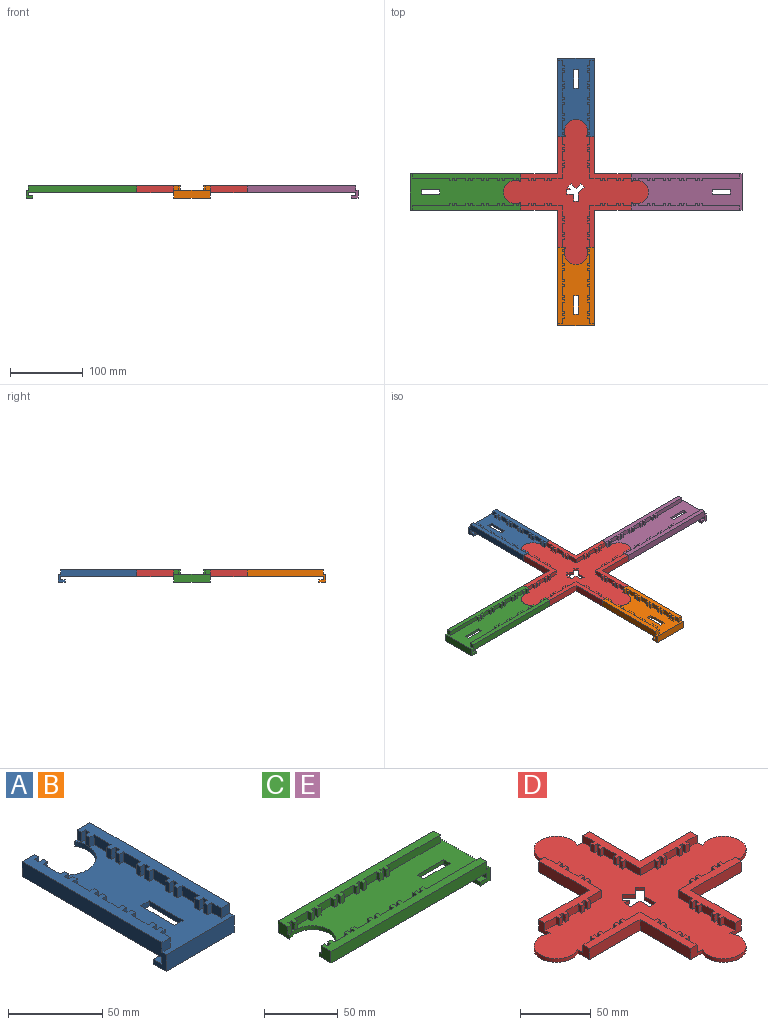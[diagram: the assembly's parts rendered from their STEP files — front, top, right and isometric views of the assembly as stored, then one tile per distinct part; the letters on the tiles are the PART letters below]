
ASSEMBLY  parts=5 mates=8
PART A: 100 faces, bbox 50.8x108x17.1 mm
  f0: plane 100.33x50.8mm, normal (0,0,1), area 3132.4mm2, adj f3,f4,f5,f6,f8,f10,f11,f12
  f1: plane 7.62x5.12mm, normal (0,0,1), area 14.9mm2, adj f8,f9,f94,f95,f96,f97,f98
  f2: plane 104.78x50.8mm, normal (0,0,-1), area 4533.1mm2, adj f3,f4,f5,f6,f7,f8,f9,f10
  f3: plane 25.4x3.18mm, normal (1,0,0), area 80.6mm2, adj f0,f2,f4,f12
  f4: plane 6.35x3.18mm, normal (0,-1,0), area 20.2mm2, adj f0,f2,f3,f5
  f5: plane 25.4x3.18mm, normal (-1,0,0), area 80.6mm2, adj f0,f2,f4,f12
  f6: plane 107.95x17.15mm, normal (1,0,0), area 1052.4mm2, adj f0,f2,f7,f11,f14,f15,f16,f17
  f7: plane 11.47x9.53mm, normal (0,1,0), area 96.9mm2, adj f2,f6,f8,f13,f18,f58
  f8: cylinder r=15.88mm len=31.75mm, axis (0,0,-1), area 208.8mm2, adj f0,f1,f2,f7,f9,f13
  f9: plane 11.47x9.53mm, normal (0,1,0), area 96.9mm2, adj f1,f2,f8,f10,f98,f99
  f10: plane 107.95x17.15mm, normal (-1,0,0), area 1052.4mm2, adj f0,f2,f9,f11,f14,f15,f16,f17
  f11: plane 50.8x10.8mm, normal (0,-1,0), area 548.4mm2, adj f0,f6,f10,f15
  f12: plane 6.35x3.18mm, normal (0,1,0), area 20.2mm2, adj f0,f2,f3,f5
  f13: plane 7.62x5.12mm, normal (0,0,1), area 14.9mm2, adj f7,f8,f18,f19,f20,f21,f22
  f14: plane 50.8x4.45mm, normal (0,1,0), area 225.8mm2, adj f2,f6,f10,f16
  f15: plane 50.8x9.53mm, normal (0,0,-1), area 483.9mm2, adj f6,f10,f11,f17
  f16: plane 50.8x6.35mm, normal (0,0,1), area 322.6mm2, adj f6,f10,f14,f17
  f17: plane 50.8x3.18mm, normal (0,1,0), area 161.3mm2, adj f6,f10,f15,f16
  f18: plane 6.35x3.18mm, normal (-1,0,0), area 20.2mm2, adj f7,f13,f19,f58
  f19: plane 6.35x3.18mm, normal (0,-1,0), area 20.2mm2, adj f13,f18,f20,f58
  f20: plane 6.35x3.18mm, normal (-1,0,0), area 20.2mm2, adj f13,f19,f21,f58
  f21: plane 6.35x3.18mm, normal (0,1,0), area 20.2mm2, adj f13,f20,f22,f58
  f22: plane 6.35x3.18mm, normal (-1,0,0), area 20.2mm2, adj f0,f13,f21,f23,f58
  f23: plane 6.35x3.18mm, normal (0,-1,0), area 20.2mm2, adj f0,f22,f24,f58
  f24: plane 12.7x6.35mm, normal (-1,0,0), area 80.6mm2, adj f0,f23,f25,f58
  f25: plane 6.35x3.18mm, normal (0,1,0), area 20.2mm2, adj f0,f24,f26,f58
  f26: plane 6.35x3.18mm, normal (-1,0,0), area 20.2mm2, adj f0,f25,f27,f58
  f27: plane 6.35x3.18mm, normal (0,-1,0), area 20.2mm2, adj f0,f26,f28,f58
  f28: plane 6.35x3.18mm, normal (-1,0,0), area 20.2mm2, adj f0,f27,f29,f58
  f29: plane 6.35x3.18mm, normal (0,1,0), area 20.2mm2, adj f0,f28,f30,f58
  f30: plane 6.35x3.18mm, normal (-1,0,0), area 20.2mm2, adj f0,f29,f31,f58
  f31: plane 6.35x3.18mm, normal (0,-1,0), area 20.2mm2, adj f0,f30,f32,f58
  f32: plane 12.7x6.35mm, normal (-1,0,0), area 80.6mm2, adj f0,f31,f33,f58
  f33: plane 6.35x3.18mm, normal (0,1,0), area 20.2mm2, adj f0,f32,f34,f58
  f34: plane 6.35x3.18mm, normal (-1,0,0), area 20.2mm2, adj f0,f33,f35,f58
  f35: plane 6.35x3.18mm, normal (0,-1,0), area 20.2mm2, adj f0,f34,f36,f58
  f36: plane 6.35x3.18mm, normal (-1,0,0), area 20.2mm2, adj f0,f35,f37,f58
  f37: plane 6.35x3.18mm, normal (0,1,0), area 20.2mm2, adj f0,f36,f38,f58
  f38: plane 6.35x3.18mm, normal (-1,0,0), area 20.2mm2, adj f0,f37,f39,f58
  f39: plane 6.35x3.18mm, normal (0,-1,0), area 20.2mm2, adj f0,f38,f40,f58
  f40: plane 11.91x6.35mm, normal (-1,0,0), area 75.6mm2, adj f0,f39,f41,f58
  f41: plane 6.35x3.18mm, normal (0,1,0), area 20.2mm2, adj f0,f40,f42,f58
  f42: plane 6.35x3.18mm, normal (-1,0,0), area 20.2mm2, adj f0,f41,f43,f58
  f43: plane 6.35x3.18mm, normal (0,-1,0), area 20.2mm2, adj f0,f42,f44,f58
  f44: plane 6.35x3.18mm, normal (-1,0,0), area 20.2mm2, adj f0,f43,f45,f58
  f45: plane 6.35x3.18mm, normal (0,1,0), area 20.2mm2, adj f0,f44,f46,f58
  f46: plane 6.35x3.18mm, normal (-1,0,0), area 20.2mm2, adj f0,f45,f47,f58
  f47: plane 6.35x3.18mm, normal (0,-1,0), area 20.2mm2, adj f0,f46,f48,f58
  f48: plane 12.7x6.35mm, normal (-1,0,0), area 80.6mm2, adj f0,f47,f49,f58
  f49: plane 6.35x3.18mm, normal (0,1,0), area 20.2mm2, adj f0,f48,f50,f58
  f50: plane 6.35x3.18mm, normal (-1,0,0), area 20.2mm2, adj f0,f49,f51,f58
  f51: plane 6.35x3.18mm, normal (0,-1,0), area 20.2mm2, adj f0,f50,f52,f58
  f52: plane 6.35x3.18mm, normal (-1,0,0), area 20.2mm2, adj f0,f51,f53,f58
  f53: plane 6.35x3.18mm, normal (0,1,0), area 20.2mm2, adj f0,f52,f54,f58
  f54: plane 6.35x3.18mm, normal (-1,0,0), area 20.2mm2, adj f0,f53,f55,f58
  f55: plane 6.35x3.18mm, normal (0,-1,0), area 20.2mm2, adj f0,f54,f56,f58
  f56: plane 7.14x6.35mm, normal (-1,0,0), area 45.4mm2, adj f0,f55,f57,f58
  f57: plane 6.35x6.35mm, normal (0,-1,0), area 40.3mm2, adj f0,f6,f56,f58
  f58: plane 104.78x9.53mm, normal (0,0,1), area 766.1mm2, adj f6,f7,f18,f19,f20,f21,f22,f23
  f59: plane 6.35x6.35mm, normal (0,-1,0), area 40.3mm2, adj f0,f10,f60,f99
  f60: plane 7.14x6.35mm, normal (1,0,0), area 45.4mm2, adj f0,f59,f61,f99
  f61: plane 6.35x3.18mm, normal (0,-1,0), area 20.2mm2, adj f0,f60,f62,f99
  f62: plane 6.35x3.18mm, normal (1,0,0), area 20.2mm2, adj f0,f61,f63,f99
  f63: plane 6.35x3.18mm, normal (0,1,0), area 20.2mm2, adj f0,f62,f64,f99
  f64: plane 6.35x3.18mm, normal (1,0,0), area 20.2mm2, adj f0,f63,f65,f99
  f65: plane 6.35x3.18mm, normal (0,-1,0), area 20.2mm2, adj f0,f64,f66,f99
  f66: plane 6.35x3.18mm, normal (1,0,0), area 20.2mm2, adj f0,f65,f67,f99
  f67: plane 6.35x3.18mm, normal (0,1,0), area 20.2mm2, adj f0,f66,f68,f99
  f68: plane 12.7x6.35mm, normal (1,0,0), area 80.6mm2, adj f0,f67,f69,f99
  f69: plane 6.35x3.18mm, normal (0,-1,0), area 20.2mm2, adj f0,f68,f70,f99
  f70: plane 6.35x3.18mm, normal (1,0,0), area 20.2mm2, adj f0,f69,f71,f99
  f71: plane 6.35x3.18mm, normal (0,1,0), area 20.2mm2, adj f0,f70,f72,f99
  f72: plane 6.35x3.18mm, normal (1,0,0), area 20.2mm2, adj f0,f71,f73,f99
  f73: plane 6.35x3.18mm, normal (0,-1,0), area 20.2mm2, adj f0,f72,f74,f99
  f74: plane 6.35x3.18mm, normal (1,0,0), area 20.2mm2, adj f0,f73,f75,f99
  f75: plane 6.35x3.18mm, normal (0,1,0), area 20.2mm2, adj f0,f74,f76,f99
  f76: plane 11.91x6.35mm, normal (1,0,0), area 75.6mm2, adj f0,f75,f77,f99
  f77: plane 6.35x3.18mm, normal (0,-1,0), area 20.2mm2, adj f0,f76,f78,f99
  f78: plane 6.35x3.18mm, normal (1,0,0), area 20.2mm2, adj f0,f77,f79,f99
  f79: plane 6.35x3.18mm, normal (0,1,0), area 20.2mm2, adj f0,f78,f80,f99
  f80: plane 6.35x3.18mm, normal (1,0,0), area 20.2mm2, adj f0,f79,f81,f99
  f81: plane 6.35x3.18mm, normal (0,-1,0), area 20.2mm2, adj f0,f80,f82,f99
  f82: plane 6.35x3.18mm, normal (1,0,0), area 20.2mm2, adj f0,f81,f83,f99
  f83: plane 6.35x3.18mm, normal (0,1,0), area 20.2mm2, adj f0,f82,f84,f99
  f84: plane 12.7x6.35mm, normal (1,0,0), area 80.6mm2, adj f0,f83,f85,f99
  f85: plane 6.35x3.18mm, normal (0,-1,0), area 20.2mm2, adj f0,f84,f86,f99
  f86: plane 6.35x3.18mm, normal (1,0,0), area 20.2mm2, adj f0,f85,f87,f99
  f87: plane 6.35x3.18mm, normal (0,1,0), area 20.2mm2, adj f0,f86,f88,f99
  f88: plane 6.35x3.18mm, normal (1,0,0), area 20.2mm2, adj f0,f87,f89,f99
  f89: plane 6.35x3.18mm, normal (0,-1,0), area 20.2mm2, adj f0,f88,f90,f99
  f90: plane 6.35x3.18mm, normal (1,0,0), area 20.2mm2, adj f0,f89,f91,f99
  f91: plane 6.35x3.18mm, normal (0,1,0), area 20.2mm2, adj f0,f90,f92,f99
  f92: plane 12.7x6.35mm, normal (1,0,0), area 80.6mm2, adj f0,f91,f93,f99
  f93: plane 6.35x3.18mm, normal (0,-1,0), area 20.2mm2, adj f0,f92,f94,f99
  f94: plane 6.35x3.18mm, normal (1,0,0), area 20.2mm2, adj f0,f1,f93,f95,f99
  f95: plane 6.35x3.18mm, normal (0,1,0), area 20.2mm2, adj f1,f94,f96,f99
  f96: plane 6.35x3.18mm, normal (1,0,0), area 20.2mm2, adj f1,f95,f97,f99
  f97: plane 6.35x3.18mm, normal (0,-1,0), area 20.2mm2, adj f1,f96,f98,f99
  f98: plane 6.35x3.18mm, normal (1,0,0), area 20.2mm2, adj f1,f9,f97,f99
  f99: plane 104.78x9.53mm, normal (0,0,1), area 766.1mm2, adj f9,f10,f59,f60,f61,f62,f63,f64
PART B: same geometry as A
PART C: 100 faces, bbox 152.4x50.8x17.1 mm
  f0: plane 144.78x50.8mm, normal (0,0,1), area 4825.9mm2, adj f3,f4,f5,f6,f8,f10,f11,f12
  f1: plane 7.62x5.12mm, normal (0,0,1), area 14.9mm2, adj f8,f9,f94,f95,f96,f97,f98
  f2: plane 50.8x4.45mm, normal (-1,0,0), area 225.8mm2, adj f6,f10,f14,f16
  f3: plane 6.35x3.18mm, normal (1,0,0), area 20.2mm2, adj f0,f4,f12,f14
  f4: plane 25.4x3.18mm, normal (0,-1,0), area 80.6mm2, adj f0,f3,f5,f14
  f5: plane 6.35x3.18mm, normal (-1,0,0), area 20.2mm2, adj f0,f4,f12,f14
  f6: plane 152.4x17.15mm, normal (0,1,0), area 1475.8mm2, adj f0,f2,f7,f11,f14,f15,f16,f17
  f7: plane 11.47x9.53mm, normal (-1,0,0), area 96.9mm2, adj f6,f8,f13,f14,f19,f58
  f8: cylinder r=15.88mm len=31.75mm, axis (0,0,-1), area 208.8mm2, adj f0,f1,f7,f9,f13,f14
  f9: plane 11.47x9.53mm, normal (-1,0,0), area 96.9mm2, adj f1,f8,f10,f14,f98,f99
  f10: plane 152.4x17.15mm, normal (0,-1,0), area 1475.8mm2, adj f0,f2,f9,f11,f14,f15,f16,f17
  f11: plane 50.8x10.8mm, normal (1,0,0), area 548.4mm2, adj f0,f6,f10,f15
  f12: plane 25.4x3.18mm, normal (0,1,0), area 80.6mm2, adj f0,f3,f5,f14
  f13: plane 7.62x5.12mm, normal (0,0,1), area 14.9mm2, adj f7,f8,f19,f20,f21,f22,f23
  f14: plane 149.23x50.8mm, normal (0,0,-1), area 6791.2mm2, adj f2,f3,f4,f5,f6,f7,f8,f9
  f15: plane 50.8x9.53mm, normal (0,0,-1), area 483.9mm2, adj f6,f10,f11,f17
  f16: plane 50.8x6.35mm, normal (0,0,1), area 322.6mm2, adj f2,f6,f10,f17
  f17: plane 50.8x3.18mm, normal (-1,0,0), area 161.3mm2, adj f6,f10,f15,f16
  f18: plane 6.35x6.35mm, normal (1,0,0), area 40.3mm2, adj f0,f6,f57,f58
  f19: plane 6.35x3.18mm, normal (0,-1,0), area 20.2mm2, adj f7,f13,f20,f58
  f20: plane 6.35x3.18mm, normal (1,0,0), area 20.2mm2, adj f13,f19,f21,f58
  f21: plane 6.35x3.18mm, normal (0,-1,0), area 20.2mm2, adj f13,f20,f22,f58
  f22: plane 6.35x3.18mm, normal (-1,0,0), area 20.2mm2, adj f13,f21,f23,f58
  f23: plane 6.35x3.18mm, normal (0,-1,0), area 20.2mm2, adj f0,f13,f22,f24,f58
  f24: plane 6.35x3.18mm, normal (1,0,0), area 20.2mm2, adj f0,f23,f25,f58
  f25: plane 12.7x6.35mm, normal (0,-1,0), area 80.6mm2, adj f0,f24,f26,f58
  f26: plane 6.35x3.18mm, normal (-1,0,0), area 20.2mm2, adj f0,f25,f27,f58
  f27: plane 6.35x3.18mm, normal (0,-1,0), area 20.2mm2, adj f0,f26,f28,f58
  f28: plane 6.35x3.18mm, normal (1,0,0), area 20.2mm2, adj f0,f27,f29,f58
  f29: plane 6.35x3.18mm, normal (0,-1,0), area 20.2mm2, adj f0,f28,f30,f58
  f30: plane 6.35x3.18mm, normal (-1,0,0), area 20.2mm2, adj f0,f29,f31,f58
  f31: plane 6.35x3.18mm, normal (0,-1,0), area 20.2mm2, adj f0,f30,f32,f58
  f32: plane 6.35x3.18mm, normal (1,0,0), area 20.2mm2, adj f0,f31,f33,f58
  f33: plane 12.7x6.35mm, normal (0,-1,0), area 80.6mm2, adj f0,f32,f34,f58
  f34: plane 6.35x3.18mm, normal (-1,0,0), area 20.2mm2, adj f0,f33,f35,f58
  f35: plane 6.35x3.18mm, normal (0,-1,0), area 20.2mm2, adj f0,f34,f36,f58
  f36: plane 6.35x3.18mm, normal (1,0,0), area 20.2mm2, adj f0,f35,f37,f58
  f37: plane 6.35x3.18mm, normal (0,-1,0), area 20.2mm2, adj f0,f36,f38,f58
  f38: plane 6.35x3.18mm, normal (-1,0,0), area 20.2mm2, adj f0,f37,f39,f58
  f39: plane 6.35x3.18mm, normal (0,-1,0), area 20.2mm2, adj f0,f38,f40,f58
  f40: plane 6.35x3.18mm, normal (1,0,0), area 20.2mm2, adj f0,f39,f41,f58
  f41: plane 11.91x6.35mm, normal (0,-1,0), area 75.6mm2, adj f0,f40,f42,f58
  f42: plane 6.35x3.18mm, normal (-1,0,0), area 20.2mm2, adj f0,f41,f43,f58
  f43: plane 6.35x3.18mm, normal (0,-1,0), area 20.2mm2, adj f0,f42,f44,f58
  f44: plane 6.35x3.18mm, normal (1,0,0), area 20.2mm2, adj f0,f43,f45,f58
  f45: plane 6.35x3.18mm, normal (0,-1,0), area 20.2mm2, adj f0,f44,f46,f58
  f46: plane 6.35x3.18mm, normal (-1,0,0), area 20.2mm2, adj f0,f45,f47,f58
  f47: plane 6.35x3.18mm, normal (0,-1,0), area 20.2mm2, adj f0,f46,f48,f58
  f48: plane 6.35x3.18mm, normal (1,0,0), area 20.2mm2, adj f0,f47,f49,f58
  f49: plane 12.7x6.35mm, normal (0,-1,0), area 80.6mm2, adj f0,f48,f50,f58
  f50: plane 6.35x3.18mm, normal (-1,0,0), area 20.2mm2, adj f0,f49,f51,f58
  f51: plane 6.35x3.18mm, normal (0,-1,0), area 20.2mm2, adj f0,f50,f52,f58
  f52: plane 6.35x3.18mm, normal (1,0,0), area 20.2mm2, adj f0,f51,f53,f58
  f53: plane 6.35x3.18mm, normal (0,-1,0), area 20.2mm2, adj f0,f52,f54,f58
  f54: plane 6.35x3.18mm, normal (-1,0,0), area 20.2mm2, adj f0,f53,f55,f58
  f55: plane 6.35x3.18mm, normal (0,-1,0), area 20.2mm2, adj f0,f54,f56,f58
  f56: plane 6.35x3.18mm, normal (1,0,0), area 20.2mm2, adj f0,f55,f57,f58
  f57: plane 51.59x6.35mm, normal (0,-1,0), area 327.6mm2, adj f0,f18,f56,f58
  f58: plane 149.23x9.53mm, normal (0,0,1), area 1048.4mm2, adj f6,f7,f18,f19,f20,f21,f22,f23
  f59: plane 6.35x6.35mm, normal (1,0,0), area 40.3mm2, adj f0,f10,f60,f99
  f60: plane 51.59x6.35mm, normal (0,1,0), area 327.6mm2, adj f0,f59,f61,f99
  f61: plane 6.35x3.18mm, normal (1,0,0), area 20.2mm2, adj f0,f60,f62,f99
  f62: plane 6.35x3.18mm, normal (0,1,0), area 20.2mm2, adj f0,f61,f63,f99
  f63: plane 6.35x3.18mm, normal (-1,0,0), area 20.2mm2, adj f0,f62,f64,f99
  f64: plane 6.35x3.18mm, normal (0,1,0), area 20.2mm2, adj f0,f63,f65,f99
  f65: plane 6.35x3.18mm, normal (1,0,0), area 20.2mm2, adj f0,f64,f66,f99
  f66: plane 6.35x3.18mm, normal (0,1,0), area 20.2mm2, adj f0,f65,f67,f99
  f67: plane 6.35x3.18mm, normal (-1,0,0), area 20.2mm2, adj f0,f66,f68,f99
  f68: plane 12.7x6.35mm, normal (0,1,0), area 80.6mm2, adj f0,f67,f69,f99
  f69: plane 6.35x3.18mm, normal (1,0,0), area 20.2mm2, adj f0,f68,f70,f99
  f70: plane 6.35x3.18mm, normal (0,1,0), area 20.2mm2, adj f0,f69,f71,f99
  f71: plane 6.35x3.18mm, normal (-1,0,0), area 20.2mm2, adj f0,f70,f72,f99
  f72: plane 6.35x3.18mm, normal (0,1,0), area 20.2mm2, adj f0,f71,f73,f99
  f73: plane 6.35x3.18mm, normal (1,0,0), area 20.2mm2, adj f0,f72,f74,f99
  f74: plane 6.35x3.18mm, normal (0,1,0), area 20.2mm2, adj f0,f73,f75,f99
  f75: plane 6.35x3.18mm, normal (-1,0,0), area 20.2mm2, adj f0,f74,f76,f99
  f76: plane 11.91x6.35mm, normal (0,1,0), area 75.6mm2, adj f0,f75,f77,f99
  f77: plane 6.35x3.18mm, normal (1,0,0), area 20.2mm2, adj f0,f76,f78,f99
  f78: plane 6.35x3.18mm, normal (0,1,0), area 20.2mm2, adj f0,f77,f79,f99
  f79: plane 6.35x3.18mm, normal (-1,0,0), area 20.2mm2, adj f0,f78,f80,f99
  f80: plane 6.35x3.18mm, normal (0,1,0), area 20.2mm2, adj f0,f79,f81,f99
  f81: plane 6.35x3.18mm, normal (1,0,0), area 20.2mm2, adj f0,f80,f82,f99
  f82: plane 6.35x3.18mm, normal (0,1,0), area 20.2mm2, adj f0,f81,f83,f99
  f83: plane 6.35x3.18mm, normal (-1,0,0), area 20.2mm2, adj f0,f82,f84,f99
  f84: plane 12.7x6.35mm, normal (0,1,0), area 80.6mm2, adj f0,f83,f85,f99
  f85: plane 6.35x3.18mm, normal (1,0,0), area 20.2mm2, adj f0,f84,f86,f99
  f86: plane 6.35x3.18mm, normal (0,1,0), area 20.2mm2, adj f0,f85,f87,f99
  f87: plane 6.35x3.18mm, normal (-1,0,0), area 20.2mm2, adj f0,f86,f88,f99
  f88: plane 6.35x3.18mm, normal (0,1,0), area 20.2mm2, adj f0,f87,f89,f99
  f89: plane 6.35x3.18mm, normal (1,0,0), area 20.2mm2, adj f0,f88,f90,f99
  f90: plane 6.35x3.18mm, normal (0,1,0), area 20.2mm2, adj f0,f89,f91,f99
  f91: plane 6.35x3.18mm, normal (-1,0,0), area 20.2mm2, adj f0,f90,f92,f99
  f92: plane 12.7x6.35mm, normal (0,1,0), area 80.6mm2, adj f0,f91,f93,f99
  f93: plane 6.35x3.18mm, normal (1,0,0), area 20.2mm2, adj f0,f92,f94,f99
  f94: plane 6.35x3.18mm, normal (0,1,0), area 20.2mm2, adj f0,f1,f93,f95,f99
  f95: plane 6.35x3.18mm, normal (-1,0,0), area 20.2mm2, adj f1,f94,f96,f99
  f96: plane 6.35x3.18mm, normal (0,1,0), area 20.2mm2, adj f1,f95,f97,f99
  f97: plane 6.35x3.18mm, normal (1,0,0), area 20.2mm2, adj f1,f96,f98,f99
  f98: plane 6.35x3.18mm, normal (0,1,0), area 20.2mm2, adj f1,f9,f97,f99
  f99: plane 149.23x9.53mm, normal (0,0,1), area 1048.4mm2, adj f9,f10,f59,f60,f61,f62,f63,f64
PART D: 174 faces, bbox 199.4x199.4x9.5 mm
  f0: plane 199.39x199.39mm, normal (0,0,1), area 12077.4mm2, adj f1,f2,f3,f4,f5,f6,f7,f8
  f1: plane 4.49x4.49mm, normal (-0.71,-0.71,0), area 20.2mm2, adj f0,f2,f32,f33
  f2: plane 8.05x8.05mm, normal (-0.71,0.71,0), area 36.1mm2, adj f0,f1,f3,f33
  f3: plane 11.39x3.18mm, normal (-1,0,0), area 36.1mm2, adj f0,f2,f4,f33
  f4: plane 6.35x3.18mm, normal (0,1,0), area 20.2mm2, adj f0,f3,f5,f33
  f5: plane 9.53x3.18mm, normal (1,0,0), area 30.2mm2, adj f0,f4,f6,f33
  f6: plane 9.53x3.18mm, normal (0,1,0), area 30.2mm2, adj f0,f5,f7,f33
  f7: plane 6.35x3.18mm, normal (1,0,0), area 20.2mm2, adj f0,f6,f8,f33
  f8: plane 5.04x3.18mm, normal (0,-1,0), area 16mm2, adj f0,f7,f9,f33
  f9: plane 3.56x3.56mm, normal (0.71,0.71,0), area 16mm2, adj f0,f8,f10,f33
  f10: plane 4.49x4.49mm, normal (0.71,-0.71,0), area 20.2mm2, adj f0,f9,f11,f33
  f11: plane 6.74x6.74mm, normal (-0.71,-0.71,0), area 30.2mm2, adj f0,f10,f32,f33
  f12: cylinder r=15.88mm len=31.75mm, axis (0,0,-1), area 208.8mm2, adj f0,f13,f31,f33
  f13: plane 11.47x9.53mm, normal (-1,0,0), area 76.8mm2, adj f0,f12,f14,f33,f102,f103
  f14: plane 50.8x9.53mm, normal (0,-1,0), area 483.9mm2, adj f13,f15,f33,f103
  f15: plane 50.8x9.53mm, normal (-1,0,0), area 483.9mm2, adj f14,f16,f33,f103
  f16: plane 11.47x9.53mm, normal (0,-1,0), area 76.8mm2, adj f0,f15,f17,f33,f69,f103
  f17: cylinder r=15.88mm len=31.75mm, axis (0,0,-1), area 208.8mm2, adj f0,f16,f18,f33
  f18: plane 11.47x9.53mm, normal (0,-1,0), area 76.8mm2, adj f0,f17,f19,f33,f140,f173
  f19: plane 50.8x9.53mm, normal (1,0,0), area 483.9mm2, adj f18,f20,f33,f173
  f20: plane 50.8x9.53mm, normal (0,-1,0), area 483.9mm2, adj f19,f21,f33,f173
  f21: plane 11.47x9.53mm, normal (1,0,0), area 76.8mm2, adj f0,f20,f22,f33,f141,f173
  f22: cylinder r=15.88mm len=31.75mm, axis (0,0,-1), area 208.8mm2, adj f0,f21,f23,f33
  f23: plane 11.47x9.53mm, normal (1,0,0), area 76.8mm2, adj f0,f22,f24,f33,f137,f138
  f24: plane 50.8x9.53mm, normal (0,1,0), area 483.9mm2, adj f23,f25,f33,f138
  f25: plane 50.8x9.53mm, normal (1,0,0), area 483.9mm2, adj f24,f26,f33,f138
  f26: plane 11.47x9.53mm, normal (0,1,0), area 76.8mm2, adj f0,f25,f27,f33,f104,f138
  f27: cylinder r=15.88mm len=31.75mm, axis (0,0,-1), area 208.8mm2, adj f0,f26,f28,f33
  f28: plane 11.47x9.53mm, normal (0,1,0), area 76.8mm2, adj f0,f27,f29,f33,f50,f68
  f29: plane 50.8x9.53mm, normal (-1,0,0), area 483.9mm2, adj f28,f30,f33,f68
  f30: plane 50.8x9.53mm, normal (0,1,0), area 483.9mm2, adj f29,f31,f33,f68
  f31: plane 11.47x9.53mm, normal (-1,0,0), area 76.8mm2, adj f0,f12,f30,f33,f51,f68
  f32: plane 6.74x6.74mm, normal (0.71,-0.71,0), area 30.2mm2, adj f0,f1,f11,f33
  f33: plane 199.39x199.39mm, normal (0,0,-1), area 15141.9mm2, adj f1,f2,f3,f4,f5,f6,f7,f8
  f34: plane 14.29x6.35mm, normal (1,0,0), area 90.7mm2, adj f0,f35,f67,f68
  f35: plane 6.35x3.18mm, normal (0,-1,0), area 20.2mm2, adj f0,f34,f36,f68
  f36: plane 6.35x3.18mm, normal (1,0,0), area 20.2mm2, adj f0,f35,f37,f68
  f37: plane 6.35x3.18mm, normal (0,1,0), area 20.2mm2, adj f0,f36,f38,f68
  f38: plane 6.35x3.18mm, normal (1,0,0), area 20.2mm2, adj f0,f37,f39,f68
  f39: plane 6.35x3.18mm, normal (0,-1,0), area 20.2mm2, adj f0,f38,f40,f68
  f40: plane 6.35x3.18mm, normal (1,0,0), area 20.2mm2, adj f0,f39,f41,f68
  f41: plane 6.35x3.18mm, normal (0,1,0), area 20.2mm2, adj f0,f40,f42,f68
  f42: plane 12.7x6.35mm, normal (1,0,0), area 80.6mm2, adj f0,f41,f43,f68
  f43: plane 6.35x3.18mm, normal (0,-1,0), area 20.2mm2, adj f0,f42,f44,f68
  f44: plane 6.35x3.18mm, normal (1,0,0), area 20.2mm2, adj f0,f43,f45,f68
  f45: plane 6.35x3.18mm, normal (0,1,0), area 20.2mm2, adj f0,f44,f46,f68
  f46: plane 6.35x3.18mm, normal (1,0,0), area 20.2mm2, adj f0,f45,f47,f68
  f47: plane 6.35x3.18mm, normal (0,-1,0), area 20.2mm2, adj f0,f46,f48,f68
  f48: plane 6.35x3.18mm, normal (1,0,0), area 20.2mm2, adj f0,f47,f49,f68
  f49: plane 6.35x3.18mm, normal (0,1,0), area 20.2mm2, adj f0,f48,f50,f68
  f50: plane 11.11x6.35mm, normal (1,0,0), area 70.6mm2, adj f0,f28,f49,f68
  f51: plane 11.11x6.35mm, normal (0,-1,0), area 70.6mm2, adj f0,f31,f52,f68
  f52: plane 6.35x3.18mm, normal (-1,0,0), area 20.2mm2, adj f0,f51,f53,f68
  f53: plane 6.35x3.18mm, normal (0,-1,0), area 20.2mm2, adj f0,f52,f54,f68
  f54: plane 6.35x3.18mm, normal (1,0,0), area 20.2mm2, adj f0,f53,f55,f68
  f55: plane 6.35x3.18mm, normal (0,-1,0), area 20.2mm2, adj f0,f54,f56,f68
  f56: plane 6.35x3.18mm, normal (-1,0,0), area 20.2mm2, adj f0,f55,f57,f68
  f57: plane 6.35x3.18mm, normal (0,-1,0), area 20.2mm2, adj f0,f56,f58,f68
  f58: plane 6.35x3.18mm, normal (1,0,0), area 20.2mm2, adj f0,f57,f59,f68
  f59: plane 12.7x6.35mm, normal (0,-1,0), area 80.6mm2, adj f0,f58,f60,f68
  f60: plane 6.35x3.18mm, normal (-1,0,0), area 20.2mm2, adj f0,f59,f61,f68
  f61: plane 6.35x3.18mm, normal (0,-1,0), area 20.2mm2, adj f0,f60,f62,f68
  f62: plane 6.35x3.18mm, normal (1,0,0), area 20.2mm2, adj f0,f61,f63,f68
  f63: plane 6.35x3.18mm, normal (0,-1,0), area 20.2mm2, adj f0,f62,f64,f68
  f64: plane 6.35x3.18mm, normal (-1,0,0), area 20.2mm2, adj f0,f63,f65,f68
  f65: plane 6.35x3.18mm, normal (0,-1,0), area 20.2mm2, adj f0,f64,f66,f68
  f66: plane 6.35x3.18mm, normal (1,0,0), area 20.2mm2, adj f0,f65,f67,f68
  f67: plane 14.29x6.35mm, normal (0,-1,0), area 90.7mm2, adj f0,f34,f66,f68
  f68: plane 60.33x60.33mm, normal (0,0,1), area 766.1mm2, adj f28,f29,f30,f31,f34,f35,f36,f37
  f69: plane 11.11x6.35mm, normal (1,0,0), area 70.6mm2, adj f0,f16,f70,f103
  f70: plane 6.35x3.18mm, normal (0,-1,0), area 20.2mm2, adj f0,f69,f71,f103
  f71: plane 6.35x3.18mm, normal (1,0,0), area 20.2mm2, adj f0,f70,f72,f103
  f72: plane 6.35x3.18mm, normal (0,1,0), area 20.2mm2, adj f0,f71,f73,f103
  f73: plane 6.35x3.18mm, normal (1,0,0), area 20.2mm2, adj f0,f72,f74,f103
  f74: plane 6.35x3.18mm, normal (0,-1,0), area 20.2mm2, adj f0,f73,f75,f103
  f75: plane 6.35x3.18mm, normal (1,0,0), area 20.2mm2, adj f0,f74,f76,f103
  f76: plane 6.35x3.18mm, normal (0,1,0), area 20.2mm2, adj f0,f75,f77,f103
  f77: plane 12.7x6.35mm, normal (1,0,0), area 80.6mm2, adj f0,f76,f78,f103
  f78: plane 6.35x3.18mm, normal (0,-1,0), area 20.2mm2, adj f0,f77,f79,f103
  f79: plane 6.35x3.18mm, normal (1,0,0), area 20.2mm2, adj f0,f78,f80,f103
  f80: plane 6.35x3.18mm, normal (0,1,0), area 20.2mm2, adj f0,f79,f81,f103
  f81: plane 6.35x3.18mm, normal (1,0,0), area 20.2mm2, adj f0,f80,f82,f103
  f82: plane 6.35x3.18mm, normal (0,-1,0), area 20.2mm2, adj f0,f81,f83,f103
  f83: plane 6.35x3.18mm, normal (1,0,0), area 20.2mm2, adj f0,f82,f84,f103
  f84: plane 6.35x3.18mm, normal (0,1,0), area 20.2mm2, adj f0,f83,f85,f103
  f85: plane 14.29x6.35mm, normal (1,0,0), area 90.7mm2, adj f0,f84,f86,f103
  f86: plane 14.29x6.35mm, normal (0,1,0), area 90.7mm2, adj f0,f85,f87,f103
  f87: plane 6.35x3.18mm, normal (1,0,0), area 20.2mm2, adj f0,f86,f88,f103
  f88: plane 6.35x3.18mm, normal (0,1,0), area 20.2mm2, adj f0,f87,f89,f103
  f89: plane 6.35x3.18mm, normal (-1,0,0), area 20.2mm2, adj f0,f88,f90,f103
  f90: plane 6.35x3.18mm, normal (0,1,0), area 20.2mm2, adj f0,f89,f91,f103
  f91: plane 6.35x3.18mm, normal (1,0,0), area 20.2mm2, adj f0,f90,f92,f103
  f92: plane 6.35x3.18mm, normal (0,1,0), area 20.2mm2, adj f0,f91,f93,f103
  f93: plane 6.35x3.18mm, normal (-1,0,0), area 20.2mm2, adj f0,f92,f94,f103
  f94: plane 12.7x6.35mm, normal (0,1,0), area 80.6mm2, adj f0,f93,f95,f103
  f95: plane 6.35x3.18mm, normal (1,0,0), area 20.2mm2, adj f0,f94,f96,f103
  f96: plane 6.35x3.18mm, normal (0,1,0), area 20.2mm2, adj f0,f95,f97,f103
  f97: plane 6.35x3.18mm, normal (-1,0,0), area 20.2mm2, adj f0,f96,f98,f103
  f98: plane 6.35x3.18mm, normal (0,1,0), area 20.2mm2, adj f0,f97,f99,f103
  f99: plane 6.35x3.18mm, normal (1,0,0), area 20.2mm2, adj f0,f98,f100,f103
  f100: plane 6.35x3.18mm, normal (0,1,0), area 20.2mm2, adj f0,f99,f101,f103
  f101: plane 6.35x3.18mm, normal (-1,0,0), area 20.2mm2, adj f0,f100,f102,f103
  f102: plane 11.11x6.35mm, normal (0,1,0), area 70.6mm2, adj f0,f13,f101,f103
  f103: plane 60.33x60.33mm, normal (0,0,1), area 766.1mm2, adj f13,f14,f15,f16,f69,f70,f71,f72
  f104: plane 11.11x6.35mm, normal (-1,0,0), area 70.6mm2, adj f0,f26,f105,f138
  f105: plane 6.35x3.18mm, normal (0,1,0), area 20.2mm2, adj f0,f104,f106,f138
  f106: plane 6.35x3.18mm, normal (-1,0,0), area 20.2mm2, adj f0,f105,f107,f138
  f107: plane 6.35x3.18mm, normal (0,-1,0), area 20.2mm2, adj f0,f106,f108,f138
  f108: plane 6.35x3.18mm, normal (-1,0,0), area 20.2mm2, adj f0,f107,f109,f138
  f109: plane 6.35x3.18mm, normal (0,1,0), area 20.2mm2, adj f0,f108,f110,f138
  f110: plane 6.35x3.18mm, normal (-1,0,0), area 20.2mm2, adj f0,f109,f111,f138
  f111: plane 6.35x3.18mm, normal (0,-1,0), area 20.2mm2, adj f0,f110,f112,f138
  f112: plane 12.7x6.35mm, normal (-1,0,0), area 80.6mm2, adj f0,f111,f113,f138
  f113: plane 6.35x3.18mm, normal (0,1,0), area 20.2mm2, adj f0,f112,f114,f138
  f114: plane 6.35x3.18mm, normal (-1,0,0), area 20.2mm2, adj f0,f113,f115,f138
  f115: plane 6.35x3.18mm, normal (0,-1,0), area 20.2mm2, adj f0,f114,f116,f138
  f116: plane 6.35x3.18mm, normal (-1,0,0), area 20.2mm2, adj f0,f115,f117,f138
  f117: plane 6.35x3.18mm, normal (0,1,0), area 20.2mm2, adj f0,f116,f118,f138
  f118: plane 6.35x3.18mm, normal (-1,0,0), area 20.2mm2, adj f0,f117,f119,f138
  f119: plane 6.35x3.18mm, normal (0,-1,0), area 20.2mm2, adj f0,f118,f120,f138
  f120: plane 14.29x6.35mm, normal (-1,0,0), area 90.7mm2, adj f0,f119,f121,f138
  f121: plane 14.29x6.35mm, normal (0,-1,0), area 90.7mm2, adj f0,f120,f122,f138
  f122: plane 6.35x3.18mm, normal (-1,0,0), area 20.2mm2, adj f0,f121,f123,f138
  f123: plane 6.35x3.18mm, normal (0,-1,0), area 20.2mm2, adj f0,f122,f124,f138
  f124: plane 6.35x3.18mm, normal (1,0,0), area 20.2mm2, adj f0,f123,f125,f138
  f125: plane 6.35x3.18mm, normal (0,-1,0), area 20.2mm2, adj f0,f124,f126,f138
  f126: plane 6.35x3.18mm, normal (-1,0,0), area 20.2mm2, adj f0,f125,f127,f138
  f127: plane 6.35x3.18mm, normal (0,-1,0), area 20.2mm2, adj f0,f126,f128,f138
  f128: plane 6.35x3.18mm, normal (1,0,0), area 20.2mm2, adj f0,f127,f129,f138
  f129: plane 12.7x6.35mm, normal (0,-1,0), area 80.6mm2, adj f0,f128,f130,f138
  f130: plane 6.35x3.18mm, normal (-1,0,0), area 20.2mm2, adj f0,f129,f131,f138
  f131: plane 6.35x3.18mm, normal (0,-1,0), area 20.2mm2, adj f0,f130,f132,f138
  f132: plane 6.35x3.18mm, normal (1,0,0), area 20.2mm2, adj f0,f131,f133,f138
  f133: plane 6.35x3.18mm, normal (0,-1,0), area 20.2mm2, adj f0,f132,f134,f138
  f134: plane 6.35x3.18mm, normal (-1,0,0), area 20.2mm2, adj f0,f133,f135,f138
  f135: plane 6.35x3.18mm, normal (0,-1,0), area 20.2mm2, adj f0,f134,f136,f138
  f136: plane 6.35x3.18mm, normal (1,0,0), area 20.2mm2, adj f0,f135,f137,f138
  f137: plane 11.11x6.35mm, normal (0,-1,0), area 70.6mm2, adj f0,f23,f136,f138
  f138: plane 60.33x60.33mm, normal (0,0,1), area 766.1mm2, adj f23,f24,f25,f26,f104,f105,f106,f107
  f139: plane 6.35x3.18mm, normal (0,-1,0), area 20.2mm2, adj f0,f140,f172,f173
  f140: plane 11.11x6.35mm, normal (-1,0,0), area 70.6mm2, adj f0,f18,f139,f173
  f141: plane 11.11x6.35mm, normal (0,1,0), area 70.6mm2, adj f0,f21,f142,f173
  f142: plane 6.35x3.18mm, normal (1,0,0), area 20.2mm2, adj f0,f141,f143,f173
  f143: plane 6.35x3.18mm, normal (0,1,0), area 20.2mm2, adj f0,f142,f144,f173
  f144: plane 6.35x3.18mm, normal (-1,0,0), area 20.2mm2, adj f0,f143,f145,f173
  f145: plane 6.35x3.18mm, normal (0,1,0), area 20.2mm2, adj f0,f144,f146,f173
  f146: plane 6.35x3.18mm, normal (1,0,0), area 20.2mm2, adj f0,f145,f147,f173
  f147: plane 6.35x3.18mm, normal (0,1,0), area 20.2mm2, adj f0,f146,f148,f173
  f148: plane 6.35x3.18mm, normal (-1,0,0), area 20.2mm2, adj f0,f147,f149,f173
  f149: plane 12.7x6.35mm, normal (0,1,0), area 80.6mm2, adj f0,f148,f150,f173
  f150: plane 6.35x3.18mm, normal (1,0,0), area 20.2mm2, adj f0,f149,f151,f173
  f151: plane 6.35x3.18mm, normal (0,1,0), area 20.2mm2, adj f0,f150,f152,f173
  f152: plane 6.35x3.18mm, normal (-1,0,0), area 20.2mm2, adj f0,f151,f153,f173
  f153: plane 6.35x3.18mm, normal (0,1,0), area 20.2mm2, adj f0,f152,f154,f173
  f154: plane 6.35x3.18mm, normal (1,0,0), area 20.2mm2, adj f0,f153,f155,f173
  f155: plane 6.35x3.18mm, normal (0,1,0), area 20.2mm2, adj f0,f154,f156,f173
  f156: plane 6.35x3.18mm, normal (-1,0,0), area 20.2mm2, adj f0,f155,f157,f173
  f157: plane 14.29x6.35mm, normal (0,1,0), area 90.7mm2, adj f0,f156,f158,f173
  f158: plane 14.29x6.35mm, normal (-1,0,0), area 90.7mm2, adj f0,f157,f159,f173
  f159: plane 6.35x3.18mm, normal (0,1,0), area 20.2mm2, adj f0,f158,f160,f173
  f160: plane 6.35x3.18mm, normal (-1,0,0), area 20.2mm2, adj f0,f159,f161,f173
  f161: plane 6.35x3.18mm, normal (0,-1,0), area 20.2mm2, adj f0,f160,f162,f173
  f162: plane 6.35x3.18mm, normal (-1,0,0), area 20.2mm2, adj f0,f161,f163,f173
  f163: plane 6.35x3.18mm, normal (0,1,0), area 20.2mm2, adj f0,f162,f164,f173
  f164: plane 6.35x3.18mm, normal (-1,0,0), area 20.2mm2, adj f0,f163,f165,f173
  f165: plane 6.35x3.18mm, normal (0,-1,0), area 20.2mm2, adj f0,f164,f166,f173
  f166: plane 12.7x6.35mm, normal (-1,0,0), area 80.6mm2, adj f0,f165,f167,f173
  f167: plane 6.35x3.18mm, normal (0,1,0), area 20.2mm2, adj f0,f166,f168,f173
  f168: plane 6.35x3.18mm, normal (-1,0,0), area 20.2mm2, adj f0,f167,f169,f173
  f169: plane 6.35x3.18mm, normal (0,-1,0), area 20.2mm2, adj f0,f168,f170,f173
  f170: plane 6.35x3.18mm, normal (-1,0,0), area 20.2mm2, adj f0,f169,f171,f173
  f171: plane 6.35x3.18mm, normal (0,1,0), area 20.2mm2, adj f0,f170,f172,f173
  f172: plane 6.35x3.18mm, normal (-1,0,0), area 20.2mm2, adj f0,f139,f171,f173
  f173: plane 60.33x60.33mm, normal (0,0,1), area 766.1mm2, adj f18,f19,f20,f21,f139,f140,f141,f142
PART E: same geometry as C
PLACE A rot(axis=(0,0,1),180deg) t=(437.3,-13.42,23.43)mm
PLACE B t=(437.3,-13.42,23.43)mm
PLACE C rot(axis=(0,0,1),180deg) t=(437.3,-13.42,23.43)mm
PLACE D t=(437.3,-13.42,23.43)mm
PLACE E t=(437.3,-13.42,23.43)mm
MATE cylindrical E.f8 <-> D.f22  axis (0,0,-1) through (521.12,-13.42,26.61)mm
MATE planar C.f14 <-> D.f33  axis (0,0,-1) through (281.72,-13.42,23.43)mm
MATE cylindrical C.f8 <-> D.f12  axis (0,0,-1) through (353.48,-13.42,25.02)mm
MATE planar D.f33 <-> A.f2  axis (0,0,-1) through (451.23,62.78,23.43)mm
MATE cylindrical A.f8 <-> D.f27  axis (0,0,-1) through (437.3,70.4,23.43)mm
MATE planar E.f14 <-> D.f33  axis (0,0,-1) through (592.87,-13.42,23.43)mm
MATE planar B.f2 <-> D.f33  axis (0,0,-1) through (437.3,-146.85,23.43)mm
MATE cylindrical D.f17 <-> B.f8  axis (0,0,-1) through (437.3,-97.24,25.02)mm
